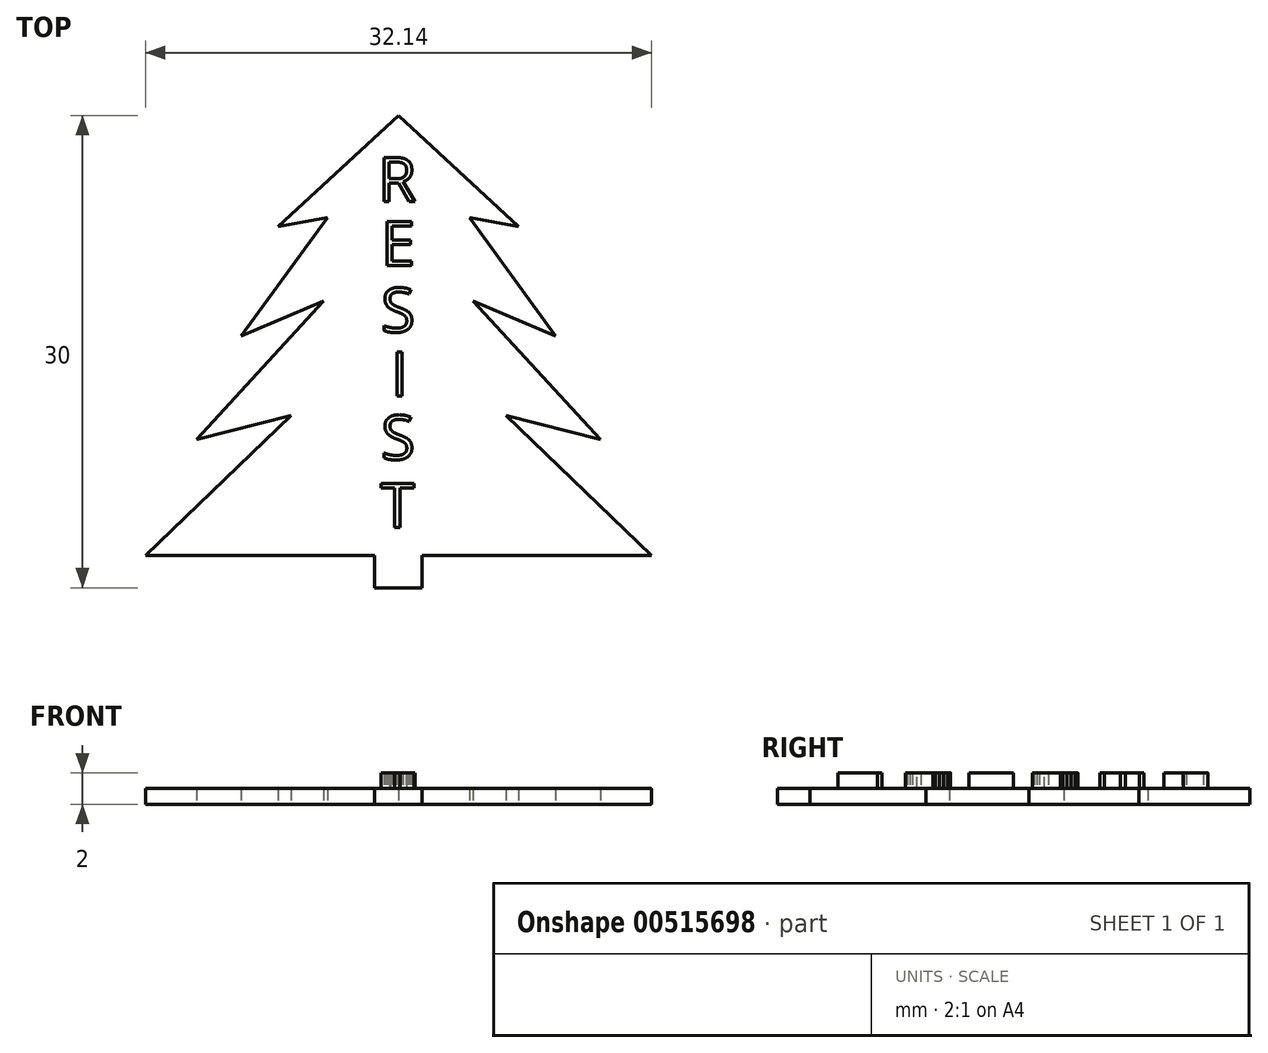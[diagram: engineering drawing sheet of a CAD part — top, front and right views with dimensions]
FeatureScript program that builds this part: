
annotation { "Feature Type Name" : "Feature", "Feature Type Description" : "" }
export const myFeature = defineFeature(function(context is Context, id is Id, definition is map)
    precondition{}
    {
        {
            var Q0;
            Q0=qCreatedBy(makeId("Top.planeOp"),FACE);
            var sketch = newSketch(context, id + "F0", { "sketchPlane" : qUnion([Q0])});
            skLineSegment(sketch, "E0", {"start": v(0, 30) * mm, "end": v(-7.63, 22.95) * mm});
            skLineSegment(sketch, "E1", {"start": v(-13.72, 2.06) * mm, "end": v(-1.5, 2.06) * mm});
            skLineSegment(sketch, "E2", {"start": v(-1.5, 2.06) * mm, "end": v(-1.5, 0) * mm});
            skLineSegment(sketch, "E3", {"start": v(-1.5, 0) * mm, "end": v(0, 0) * mm});
            skLineSegment(sketch, "E4", {"start": v(-4.51, 23.53) * mm, "end": v(-9.98, 15.99) * mm});
            skLineSegment(sketch, "E5", {"start": v(0, 0) * mm, "end": v(0, 30) * mm, "construction": true});
            skLineSegment(sketch, "E6.MirrorCS", {"start": v(0, 30) * mm, "end": v(7.63, 22.95) * mm});
            skLineSegment(sketch, "E7.MirrorCS", {"start": v(4.51, 23.53) * mm, "end": v(9.98, 15.99) * mm});
            skLineSegment(sketch, "E8.MirrorCS", {"start": v(13.72, 2.06) * mm, "end": v(1.5, 2.06) * mm});
            skLineSegment(sketch, "E9.MirrorCS", {"start": v(1.5, 0) * mm, "end": v(0, 0) * mm});
            skLineSegment(sketch, "E10.MirrorCS", {"start": v(1.5, 2.06) * mm, "end": v(1.5, 0) * mm});
            skLineSegment(sketch, "E11", {"start": v(-7.63, 22.95) * mm, "end": v(-4.51, 23.53) * mm});
            skLineSegment(sketch, "E12", {"start": v(4.51, 23.53) * mm, "end": v(7.63, 22.95) * mm});
            skLineSegment(sketch, "E13", {"start": v(-9.98, 15.99) * mm, "end": v(-4.74, 18.21) * mm});
            skLineSegment(sketch, "E14", {"start": v(-4.74, 18.21) * mm, "end": v(-12.83, 9.43) * mm});
            skLineSegment(sketch, "E15", {"start": v(-12.83, 9.43) * mm, "end": v(-6.82, 10.93) * mm});
            skLineSegment(sketch, "E16", {"start": v(-6.82, 10.93) * mm, "end": v(-16.07, 2.06) * mm});
            skLineSegment(sketch, "E17", {"start": v(-16.07, 2.06) * mm, "end": v(-13.72, 2.06) * mm});
            skLineSegment(sketch, "E18.MirrorCS", {"start": v(6.82, 10.93) * mm, "end": v(16.07, 2.06) * mm});
            skLineSegment(sketch, "E19.MirrorCS", {"start": v(12.83, 9.43) * mm, "end": v(6.82, 10.93) * mm});
            skLineSegment(sketch, "E20.MirrorCS", {"start": v(4.74, 18.21) * mm, "end": v(12.83, 9.43) * mm});
            skLineSegment(sketch, "E21.MirrorCS", {"start": v(9.98, 15.99) * mm, "end": v(4.74, 18.21) * mm});
            skLineSegment(sketch, "E22.MirrorCS", {"start": v(16.07, 2.06) * mm, "end": v(13.72, 2.06) * mm});
            skSolve(sketch);
        }
        {
            var Q0;
            Q0=makeQuery(id+"F0.imprint","IMPRINT",FACE,{"disambiguationData":[TD([[makeQuery(id+"F0.imprint","IMPRINT",EDGE,{"derivedFrom":sQuery(id+"F0.wireOp",EDGE,"E0")}),1.0]])]});
            extrude(context, id + "F1", {"entities" : qUnion([Q0]), "depth" : 1 * mm, "offsetDistance" : 25 * mm});
        }
        {
            var Q0;
            Q0=makeQuery(id+"F1.opExtrude","CAP_FACE",FACE,{"disambiguationData":[OSD([sQuery(id+"F0.wireOp",EDGE,"E0"),sQuery(id+"F0.wireOp",EDGE,"E1"),sQuery(id+"F0.wireOp",EDGE,"E2"),sQuery(id+"F0.wireOp",EDGE,"E3"),sQuery(id+"F0.wireOp",EDGE,"E4"),sQuery(id+"F0.wireOp",EDGE,"E6.MirrorCS"),sQuery(id+"F0.wireOp",EDGE,"E7.MirrorCS"),sQuery(id+"F0.wireOp",EDGE,"E8.MirrorCS"),sQuery(id+"F0.wireOp",EDGE,"E9.MirrorCS"),sQuery(id+"F0.wireOp",EDGE,"E10.MirrorCS"),sQuery(id+"F0.wireOp",EDGE,"E11"),sQuery(id+"F0.wireOp",EDGE,"E12"),sQuery(id+"F0.wireOp",EDGE,"E13"),sQuery(id+"F0.wireOp",EDGE,"E14"),sQuery(id+"F0.wireOp",EDGE,"E15"),sQuery(id+"F0.wireOp",EDGE,"E16"),sQuery(id+"F0.wireOp",EDGE,"E17"),sQuery(id+"F0.wireOp",EDGE,"E18.MirrorCS"),sQuery(id+"F0.wireOp",EDGE,"E19.MirrorCS"),sQuery(id+"F0.wireOp",EDGE,"E20.MirrorCS"),sQuery(id+"F0.wireOp",EDGE,"E21.MirrorCS"),sQuery(id+"F0.wireOp",EDGE,"E22.MirrorCS")])],"isStart":false});
            var sketch = newSketch(context, id + "F2", { "sketchPlane" : qUnion([Q0])});
            skText(sketch, "E23", { "text": "R", "fontName": "OpenSans-Regular.ttf"});
            skText(sketch, "E24", { "text": "E", "fontName": "OpenSans-Regular.ttf"});
            skPoint(sketch, "E25.firstSnap0", {"position": v(-1.1, 21.88) * mm});
            skText(sketch, "E26", { "text": "I", "fontName": "OpenSans-Regular.ttf"});
            skText(sketch, "E27", { "text": "S", "fontName": "OpenSans-Regular.ttf"});
            skText(sketch, "E28", { "text": "T", "fontName": "OpenSans-Regular.ttf"});
            skLineSegment(sketch, "E29", {"start": v(0, 0) * mm, "end": v(0, 30) * mm, "construction": true});
            skText(sketch, "E30", { "text": "S", "fontName": "OpenSans-Regular.ttf"});
            const initialGuessF2  = {"E23": [-0.0013, 0.02454, 1, 0, 0.00282], "E24": [-0.0011, 0.02048, 1, 0, 0.00282], "E26": [-0.00048, 0.01218, 1, 0, 0.00282], "E27": [-0.0011, 0.01625, 1, 0, 0.00282], "E28": [-0.00115, 0.00384, 1, 0, 0.00282], "E30": [-0.0011, 0.00816, 1, 0, 0.00282]};
            skSetInitialGuess(sketch, initialGuessF2);
            skSolve(sketch);
        }
        {
            var Q0;
            Q0 = qSketchRegion(id + "F2", true);
            extrude(context, id + "F3", {"entities" : qUnion([Q0]), "operationType" : NewBodyOperationType.ADD, "depth" : 1 * mm, "offsetDistance" : 25 * mm});
        }
    });
